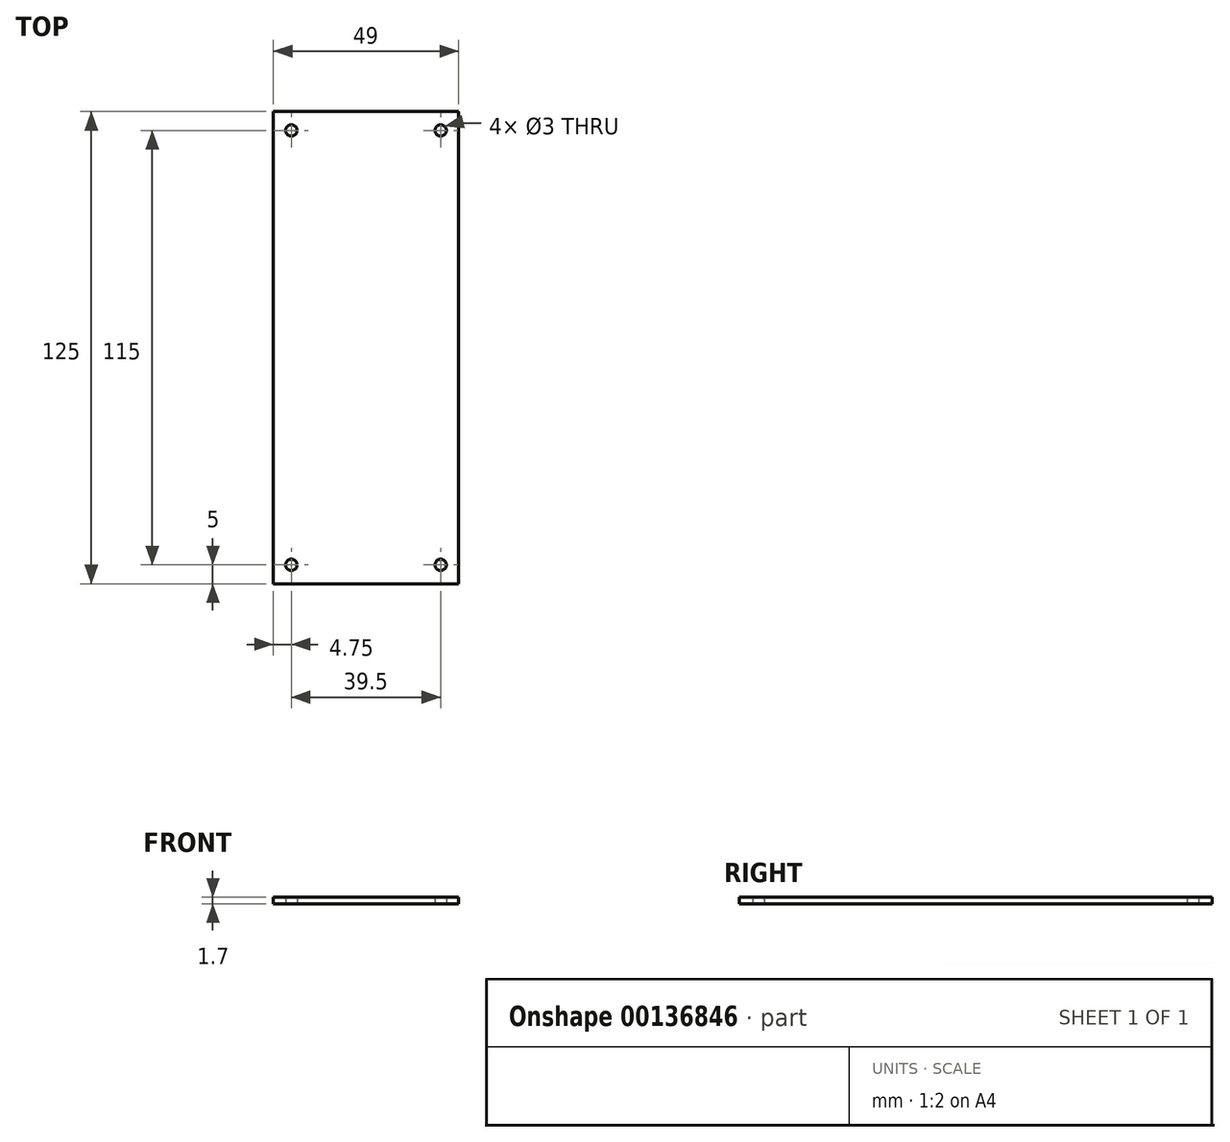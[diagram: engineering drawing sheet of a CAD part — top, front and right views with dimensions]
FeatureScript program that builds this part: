
annotation { "Feature Type Name" : "Feature", "Feature Type Description" : "" }
export const myFeature = defineFeature(function(context is Context, id is Id, definition is map)
    precondition{}
    {
        {
            var Q0;
            Q0=qCreatedBy(makeId("Top.planeOp"),FACE);
            var sketch = newSketch(context, id + "F0", { "sketchPlane" : qUnion([Q0])});
            skLineSegment(sketch, "E0.right", {"start": v(-24.5, 0) * mm, "end": v(-24.5, -62.5) * mm});
            skPoint(sketch, "E0.middle", {"position": v(0, 0) * mm});
            skCircle(sketch, "E1", {"center": v(-19.75, -57.5) * mm, "radius": 1.5 * mm});
            skLineSegment(sketch, "E2", {"start": v(-24.5, -62.5) * mm, "end": v(0, -62.5) * mm});
            skCircle(sketch, "E3.MirrorC", {"center": v(19.75, -57.5) * mm, "radius": 1.5 * mm});
            skLineSegment(sketch, "E4.MirrorCS", {"start": v(24.5, -62.5) * mm, "end": v(0, -62.5) * mm});
            skLineSegment(sketch, "E5.MirrorCS", {"start": v(24.5, 0) * mm, "end": v(24.5, -62.5) * mm});
            skCircle(sketch, "E6.MirrorC", {"center": v(19.75, 57.5) * mm, "radius": 1.5 * mm});
            skCircle(sketch, "E7.MirrorC", {"center": v(-19.75, 57.5) * mm, "radius": 1.5 * mm});
            skLineSegment(sketch, "E8.MirrorCS", {"start": v(-24.5, 62.5) * mm, "end": v(0, 62.5) * mm});
            skLineSegment(sketch, "E9.MirrorCS", {"start": v(24.5, 62.5) * mm, "end": v(0, 62.5) * mm});
            skLineSegment(sketch, "E10.MirrorCS", {"start": v(24.5, 0) * mm, "end": v(24.5, 62.5) * mm});
            skLineSegment(sketch, "E11.MirrorCS", {"start": v(-24.5, 0) * mm, "end": v(-24.5, 62.5) * mm});
            skSolve(sketch);
        }
        {
            var Q0;
            Q0=makeQuery(id+"F0.imprint","IMPRINT",FACE,{"disambiguationData":[TD([[makeQuery(id+"F0.imprint","IMPRINT",EDGE,{"derivedFrom":sQuery(id+"F0.wireOp",EDGE,"E0.right")}),1.0]])]});
            extrude(context, id + "F1", {"entities" : qUnion([Q0]), "depth" : 1.7 * mm});
        }
    });
